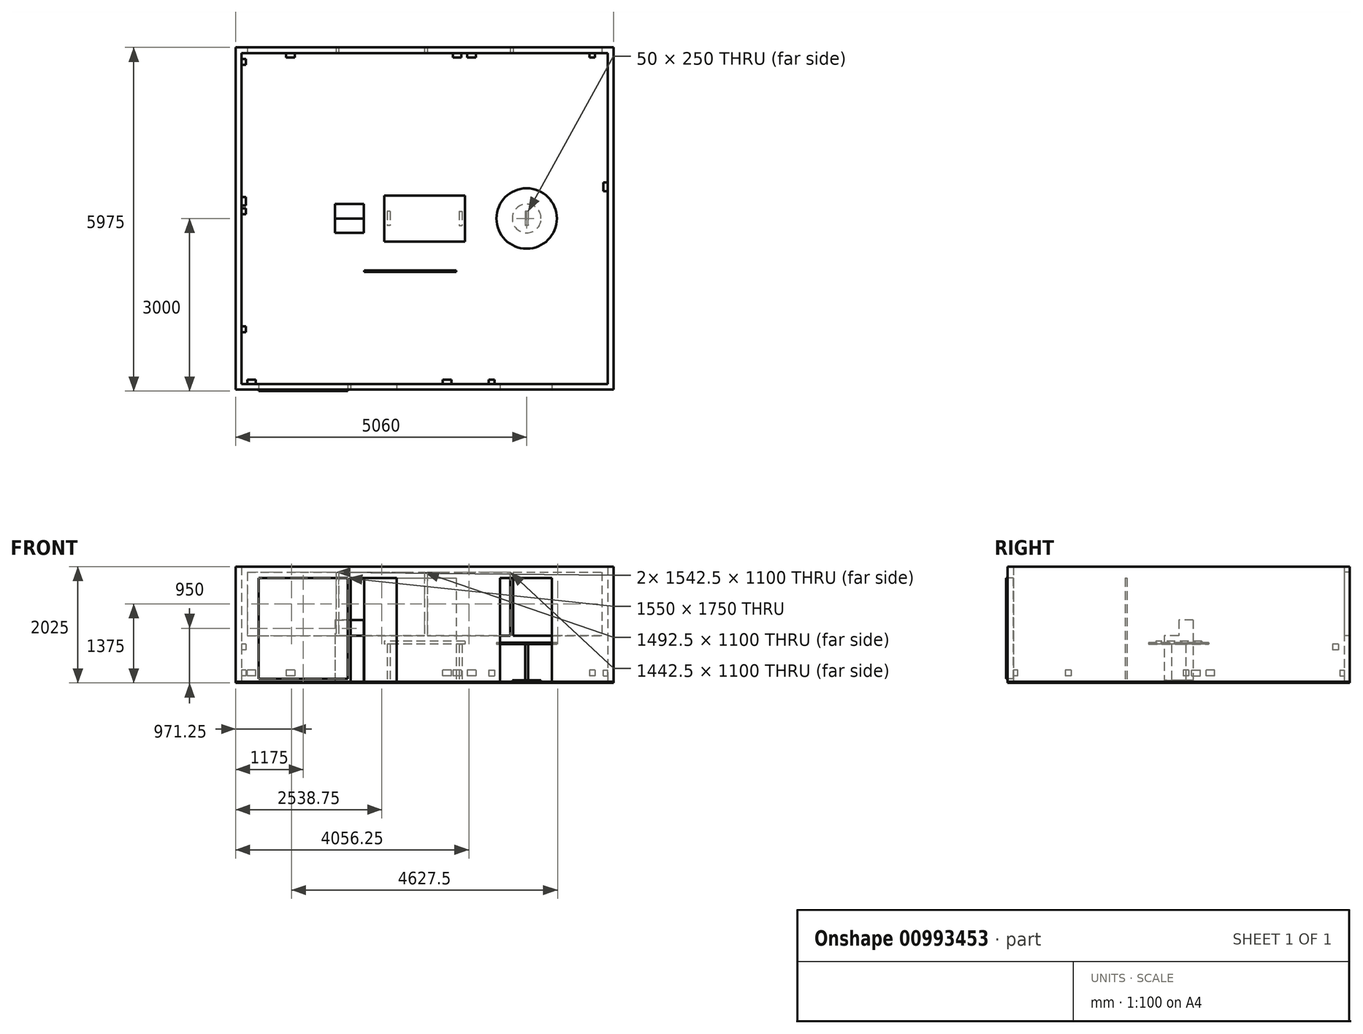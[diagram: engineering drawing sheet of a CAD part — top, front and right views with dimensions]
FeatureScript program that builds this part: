
annotation { "Feature Type Name" : "Feature", "Feature Type Description" : "" }
export const myFeature = defineFeature(function(context is Context, id is Id, definition is map)
    precondition{}
    {
        {
            var Q0;
            Q0=qCreatedBy(makeId("Top.planeOp"),FACE);
            var sketch = newSketch(context, id + "F0", { "sketchPlane" : qUnion([Q0])});
            skLineSegment(sketch, "E0.bottom", {"start": v(3185, 2875) * mm, "end": v(-3185, 2875) * mm});
            skLineSegment(sketch, "E0.top", {"start": v(3185, -2875) * mm, "end": v(-3185, -2875) * mm});
            skLineSegment(sketch, "E0.left", {"start": v(3185, 2875) * mm, "end": v(3185, -2875) * mm});
            skLineSegment(sketch, "E0.right", {"start": v(-3185, 2875) * mm, "end": v(-3185, -2875) * mm});
            skPoint(sketch, "E0.middle", {"position": v(0, 0) * mm});
            skLineSegment(sketch, "E1.0", {"start": v(3285, 2975) * mm, "end": v(-3285, 2975) * mm});
            skLineSegment(sketch, "E1.1", {"start": v(3285, 2975) * mm, "end": v(3285, -2975) * mm});
            skLineSegment(sketch, "E1.2", {"start": v(3285, -2975) * mm, "end": v(-3285, -2975) * mm});
            skLineSegment(sketch, "E1.3", {"start": v(-3285, 2975) * mm, "end": v(-3285, -2975) * mm});
            skSolve(sketch);
        }
        {
            var Q0;
            Q0=makeQuery(id+"F0.imprint","IMPRINT",FACE,{"disambiguationData":[TD([[makeQuery(id+"F0.imprint","IMPRINT",EDGE,{"derivedFrom":sQuery(id+"F0.wireOp",EDGE,"E0.bottom")}),-1.0]])]});
            extrude(context, id + "F1", {"entities" : qUnion([Q0]), "depth" : 2000 * mm, "offsetDistance" : 25 * mm});
        }
        {
            var Q0;
            Q0=makeQuery(id+"F0.imprint","IMPRINT",FACE,{"disambiguationData":[TD([[makeQuery(id+"F0.imprint","IMPRINT",EDGE,{"derivedFrom":sQuery(id+"F0.wireOp",EDGE,"E0.bottom")}),-1.0]])]});
            var Q1;
            Q1=makeQuery(id+"F0.imprint","IMPRINT",FACE,{"disambiguationData":[TD([[makeQuery(id+"F0.imprint","IMPRINT",EDGE,{"derivedFrom":sQuery(id+"F0.wireOp",EDGE,"E0.bottom")}),1.0]])]});
            extrude(context, id + "F2", {"entities" : qUnion([Q0, Q1]), "oppositeDirection" : true, "depth" : 25 * mm, "offsetDistance" : 25 * mm});
        }
        {
            var Q0;
            Q0=makeQuery(id+"F1.opExtrude","SWEPT_FACE",FACE,{"disambiguationData":[OSD([sQuery(id+"F0.wireOp",EDGE,"E1.2")])]});
            var sketch = newSketch(context, id + "F3", { "sketchPlane" : qUnion([Q0])});
            skLineSegment(sketch, "E2.bottom", {"start": v(-1285, 0) * mm, "end": v(-485, 0) * mm});
            skLineSegment(sketch, "E2.top", {"start": v(-1285, 1800) * mm, "end": v(-485, 1800) * mm});
            skLineSegment(sketch, "E2.left", {"start": v(-1285, 0) * mm, "end": v(-1285, 1800) * mm});
            skLineSegment(sketch, "E2.right", {"start": v(-485, 0) * mm, "end": v(-485, 1800) * mm});
            skLineSegment(sketch, "E3.bottom", {"start": v(1315, 0) * mm, "end": v(2215, 0) * mm});
            skLineSegment(sketch, "E3.top", {"start": v(1315, 1800) * mm, "end": v(2215, 1800) * mm});
            skLineSegment(sketch, "E3.left", {"start": v(1315, 0) * mm, "end": v(1315, 1800) * mm});
            skLineSegment(sketch, "E3.right", {"start": v(2215, 0) * mm, "end": v(2215, 1800) * mm});
            skLineSegment(sketch, "E4.bottom", {"start": v(-2885, 1800) * mm, "end": v(-1335, 1800) * mm});
            skLineSegment(sketch, "E4.top", {"start": v(-2885, 50) * mm, "end": v(-1335, 50) * mm});
            skLineSegment(sketch, "E4.left", {"start": v(-2885, 1800) * mm, "end": v(-2885, 50) * mm});
            skLineSegment(sketch, "E4.right", {"start": v(-1335, 1800) * mm, "end": v(-1335, 50) * mm});
            skSolve(sketch);
        }
        {
            var Q0;
            Q0=makeQuery(id+"F3.imprint","IMPRINT",FACE,{"disambiguationData":[TD([[makeQuery(id+"F3.imprint","IMPRINT",EDGE,{"derivedFrom":sQuery(id+"F3.wireOp",EDGE,"E2.bottom")}),-1.0]])]});
            var Q1;
            Q1=makeQuery(id+"F3.imprint","IMPRINT",FACE,{"disambiguationData":[TD([[makeQuery(id+"F3.imprint","IMPRINT",EDGE,{"derivedFrom":sQuery(id+"F3.wireOp",EDGE,"E3.bottom")}),-1.0]])]});
            var Q2;
            Q2=makeQuery(id+"F3.imprint","IMPRINT",FACE,{"disambiguationData":[TD([[makeQuery(id+"F3.imprint","IMPRINT",EDGE,{"derivedFrom":sQuery(id+"F3.wireOp",EDGE,"E4.bottom")}),-1.0]])]});
            var Q3;
            Q3=makeQuery(id+"F1.opExtrude","SWEPT_FACE",FACE,{"disambiguationData":[OSD([sQuery(id+"F0.wireOp",EDGE,"E0.top")])]});
            extrude(context, id + "F4", {"entities" : qUnion([Q0, Q1, Q2]), "operationType" : NewBodyOperationType.REMOVE, "endBound" : BoundingType.UP_TO_SURFACE, "oppositeDirection" : true, "depth" : 220 * mm, "endBoundEntityFace" : qUnion([Q3]), "offsetDistance" : 25 * mm});
        }
        {
            var Q0;
            Q0=makeQuery(id+"F3.imprint","IMPRINT",FACE,{"disambiguationData":[TD([[makeQuery(id+"F3.imprint","IMPRINT",EDGE,{"derivedFrom":sQuery(id+"F3.wireOp",EDGE,"E4.bottom")}),-1.0]])]});
            extrude(context, id + "F5", {"entities" : qUnion([Q0]), "depth" : 25 * mm, "offsetDistance" : 25 * mm});
        }
        {
            var Q0;
            Q0=makeQuery(id+"F1.opExtrude","SWEPT_FACE",FACE,{"disambiguationData":[OSD([sQuery(id+"F0.wireOp",EDGE,"E0.bottom")])]});
            var sketch = newSketch(context, id + "F6", { "sketchPlane" : qUnion([Q0])});
            skLineSegment(sketch, "E5.bottom", {"start": v(-3085, 1900) * mm, "end": v(3085, 1900) * mm});
            skLineSegment(sketch, "E5.top", {"start": v(-3085, 800) * mm, "end": v(3085, 800) * mm});
            skLineSegment(sketch, "E5.left", {"start": v(-3085, 1900) * mm, "end": v(-3085, 800) * mm});
            skLineSegment(sketch, "E5.right", {"start": v(3085, 1900) * mm, "end": v(3085, 800) * mm});
            skLineSegment(sketch, "E6", {"start": v(0, 1900) * mm, "end": v(0, 800) * mm});
            skLineSegment(sketch, "E7", {"start": v(-1542.5, 1900) * mm, "end": v(-1542.5, 800) * mm});
            skLineSegment(sketch, "E8", {"start": v(-1492.5, 1900) * mm, "end": v(-1492.5, 800) * mm});
            skLineSegment(sketch, "E9.MirrorCS", {"start": v(1492.5, 1900) * mm, "end": v(1492.5, 800) * mm});
            skLineSegment(sketch, "E10.MirrorCS", {"start": v(1542.5, 1900) * mm, "end": v(1542.5, 800) * mm});
            skLineSegment(sketch, "E11", {"start": v(50, 1900) * mm, "end": v(50, 800) * mm});
            skSolve(sketch);
        }
        {
            var Q0;
            {var subQ0=sQuery(id+"F6.wireOp",EDGE,"E5.left");Q0=makeQuery(id+"F6.imprint","IMPRINT",FACE,{"disambiguationData":[TD([[makeQuery(id+"F6.imprint","IMPRINT",EDGE,{"derivedFrom":subQ0}),1.0]])]});}
            var Q1;
            {var subQ0=sQuery(id+"F6.wireOp",EDGE,"E6");Q1=makeQuery(id+"F6.imprint","IMPRINT",FACE,{"disambiguationData":[TD([[makeQuery(id+"F6.imprint","IMPRINT",EDGE,{"derivedFrom":subQ0}),-1.0]])]});}
            var Q2;
            {var subQ0=sQuery(id+"F6.wireOp",EDGE,"E9.MirrorCS");Q2=makeQuery(id+"F6.imprint","IMPRINT",FACE,{"disambiguationData":[TD([[makeQuery(id+"F6.imprint","IMPRINT",EDGE,{"derivedFrom":subQ0}),-1.0]])]});}
            var Q3;
            {var subQ0=sQuery(id+"F6.wireOp",EDGE,"E5.right");Q3=makeQuery(id+"F6.imprint","IMPRINT",FACE,{"disambiguationData":[TD([[makeQuery(id+"F6.imprint","IMPRINT",EDGE,{"derivedFrom":subQ0}),-1.0]])]});}
            var Q4;
            Q4=makeQuery(id+"F1.opExtrude","SWEPT_FACE",FACE,{"disambiguationData":[OSD([sQuery(id+"F0.wireOp",EDGE,"E1.0")])]});
            extrude(context, id + "F7", {"entities" : qUnion([Q0, Q1, Q2, Q3]), "operationType" : NewBodyOperationType.REMOVE, "endBound" : BoundingType.UP_TO_SURFACE, "oppositeDirection" : true, "depth" : 25 * mm, "endBoundEntityFace" : qUnion([Q4]), "offsetDistance" : 25 * mm});
        }
        {
            var Q0;
            Q0=qCreatedBy(makeId("Top.planeOp"),FACE);
            var sketch = newSketch(context, id + "F8", { "sketchPlane" : qUnion([Q0])});
            skLineSegment(sketch, "E12.bottom", {"start": v(700, 400) * mm, "end": v(-700, 400) * mm, "construction": true});
            skLineSegment(sketch, "E12.top", {"start": v(700, -400) * mm, "end": v(-700, -400) * mm, "construction": true});
            skLineSegment(sketch, "E12.left", {"start": v(700, 400) * mm, "end": v(700, -400) * mm, "construction": true});
            skLineSegment(sketch, "E12.right", {"start": v(-700, 400) * mm, "end": v(-700, -400) * mm, "construction": true});
            skPoint(sketch, "E12.middle", {"position": v(0, 0) * mm});
            skLineSegment(sketch, "E13.bottom", {"start": v(-600, 125) * mm, "end": v(-650, 125) * mm});
            skLineSegment(sketch, "E13.top", {"start": v(-600, -125) * mm, "end": v(-650, -125) * mm});
            skLineSegment(sketch, "E13.left", {"start": v(-600, 125) * mm, "end": v(-600, -125) * mm});
            skLineSegment(sketch, "E13.right", {"start": v(-650, 125) * mm, "end": v(-650, -125) * mm});
            skPoint(sketch, "E13.middle", {"position": v(-625, 0) * mm});
            skPoint(sketch, "E13.middle.positionSnap0", {"position": v(-700, 0) * mm});
            skPoint(sketch, "E13.centerSnap0", {"position": v(-700, 0) * mm});
            skLineSegment(sketch, "E14.MirrorCS", {"start": v(600, 125) * mm, "end": v(600, -125) * mm});
            skLineSegment(sketch, "E15.MirrorCS", {"start": v(600, 125) * mm, "end": v(650, 125) * mm});
            skLineSegment(sketch, "E16.MirrorCS", {"start": v(650, 125) * mm, "end": v(650, -125) * mm});
            skLineSegment(sketch, "E17.MirrorCS", {"start": v(600, -125) * mm, "end": v(650, -125) * mm});
            skLineSegment(sketch, "E18.bottom", {"start": v(600, 2.5) * mm, "end": v(-600, 2.5) * mm});
            skLineSegment(sketch, "E18.top", {"start": v(600, -2.5) * mm, "end": v(-600, -2.5) * mm});
            skLineSegment(sketch, "E18.left", {"start": v(600, 2.5) * mm, "end": v(600, -2.5) * mm});
            skLineSegment(sketch, "E18.right", {"start": v(-600, 2.5) * mm, "end": v(-600, -2.5) * mm});
            skLineSegment(sketch, "E19", {"start": v(1200, 400) * mm, "end": v(1200, -400) * mm, "construction": true});
            skLineSegment(sketch, "E20.MirrorCS", {"start": v(1750, 125) * mm, "end": v(1750, -125) * mm});
            skLineSegment(sketch, "E21.MirrorCS", {"start": v(1800, 125) * mm, "end": v(1750, 125) * mm});
            skLineSegment(sketch, "E22.MirrorCS", {"start": v(1800, 125) * mm, "end": v(1800, -125) * mm});
            skLineSegment(sketch, "E23.MirrorCS", {"start": v(1800, -125) * mm, "end": v(1750, -125) * mm});
            skCircle(sketch, "E24", {"center": v(1775, 0) * mm, "radius": 250 * mm});
            skPoint(sketch, "E24.centerSnap0", {"position": v(1775, 125) * mm});
            skPoint(sketch, "E24.centerSnap1", {"position": v(1800, 0) * mm});
            skSolve(sketch);
        }
        {
            var Q0;
            {var subQ3=sQuery(id+"F8.wireOp",EDGE,"E13.bottom");Q0=makeQuery(id+"F8.imprint","IMPRINT",FACE,{"disambiguationData":[TD([[makeQuery(id+"F8.imprint","IMPRINT",EDGE,{"derivedFrom":subQ3}),1.0]])]});}
            var Q1;
            {var subQ0=sQuery(id+"F8.wireOp",EDGE,"E15.MirrorCS");Q1=makeQuery(id+"F8.imprint","IMPRINT",FACE,{"disambiguationData":[TD([[makeQuery(id+"F8.imprint","IMPRINT",EDGE,{"derivedFrom":subQ0}),-1.0]])]});}
            extrude(context, id + "F9", {"entities" : qUnion([Q0, Q1]), "depth" : 650 * mm, "offsetDistance" : 25 * mm});
        }
        {
            var Q0;
            Q0=makeQuery(id+"F9.opExtrude","CAP_FACE",FACE,{"disambiguationData":[OSD([sQuery(id+"F8.wireOp",EDGE,"E13.bottom"),sQuery(id+"F8.wireOp",EDGE,"E13.top"),sQuery(id+"F8.wireOp",EDGE,"E13.left"),sQuery(id+"F8.wireOp",EDGE,"E13.right"),sQuery(id+"F8.wireOp",EDGE,"E14.MirrorCS"),sQuery(id+"F8.wireOp",EDGE,"E15.MirrorCS"),sQuery(id+"F8.wireOp",EDGE,"E16.MirrorCS"),sQuery(id+"F8.wireOp",EDGE,"E17.MirrorCS"),sQuery(id+"F8.wireOp",EDGE,"E18.bottom"),sQuery(id+"F8.wireOp",EDGE,"E18.top")])],"isStart":false});
            var sketch = newSketch(context, id + "F10", { "sketchPlane" : qUnion([Q0])});
            skLineSegment(sketch, "E25.0", {"start": v(700, -400) * mm, "end": v(-700, -400) * mm});
            skLineSegment(sketch, "E26.0", {"start": v(-700, 400) * mm, "end": v(-700, -400) * mm});
            skLineSegment(sketch, "E27.0", {"start": v(700, 400) * mm, "end": v(-700, 400) * mm});
            skLineSegment(sketch, "E28.0", {"start": v(700, 400) * mm, "end": v(700, -400) * mm});
            skSolve(sketch);
        }
        {
            var Q0;
            Q0=makeQuery(id+"F10.imprint","IMPRINT",FACE,{"disambiguationData":[TD([[makeQuery(id+"F10.imprint","IMPRINT",EDGE,{"derivedFrom":sQuery(id+"F10.wireOp",EDGE,"E25.0")}),-1.0]])]});
            var Q1;
            {var subQ6=sQuery(id+"F8.wireOp",EDGE,"E13.bottom");Q1=makeQuery(id+"F10.imprint","IMPRINT",FACE,{"disambiguationData":[TD([[makeQuery(id+"F10.imprint","IMPRINT",EDGE,{"derivedFrom":makeQuery(id+"F9.opExtrude","CAP_EDGE",EDGE,{"disambiguationData":[OSD([subQ6])],"isStart":false})}),1.0]])]});}
            var Q2;
            Q2=makeQuery(id+"F10.imprint","IMPRINT",FACE,{"disambiguationData":[TD([[makeQuery(id+"F10.imprint","IMPRINT",EDGE,{"derivedFrom":makeQuery(id+"F9.opExtrude","CAP_EDGE",EDGE,{"disambiguationData":[OSD([sQuery(id+"F8.wireOp",EDGE,"E15.MirrorCS")])],"isStart":false})}),-1.0]])]});
            extrude(context, id + "F11", {"entities" : qUnion([Q0, Q1, Q2]), "operationType" : NewBodyOperationType.ADD, "depth" : 50 * mm, "offsetDistance" : 25 * mm});
        }
        {
            var Q0;
            Q0=makeQuery(id+"F8.imprint","IMPRINT",FACE,{"disambiguationData":[TD([[makeQuery(id+"F8.imprint","IMPRINT",EDGE,{"derivedFrom":sQuery(id+"F8.wireOp",EDGE,"E20.MirrorCS")}),1.0]])]});
            extrude(context, id + "F12", {"entities" : qUnion([Q0]), "depth" : 650 * mm, "offsetDistance" : 25 * mm});
        }
        {
            var Q0;
            Q0=makeQuery(id+"F8.imprint","IMPRINT",FACE,{"disambiguationData":[TD([[makeQuery(id+"F8.imprint","IMPRINT",EDGE,{"derivedFrom":sQuery(id+"F8.wireOp",EDGE,"E20.MirrorCS")}),-1.0]])]});
            extrude(context, id + "F13", {"entities" : qUnion([Q0]), "operationType" : NewBodyOperationType.ADD, "depth" : 25 * mm, "offsetDistance" : 25 * mm});
        }
        {
            var Q0;
            Q0=makeQuery(id+"F12.opExtrude","CAP_FACE",FACE,{"disambiguationData":[OSD([sQuery(id+"F8.wireOp",EDGE,"E20.MirrorCS"),sQuery(id+"F8.wireOp",EDGE,"E21.MirrorCS"),sQuery(id+"F8.wireOp",EDGE,"E22.MirrorCS"),sQuery(id+"F8.wireOp",EDGE,"E23.MirrorCS")])],"isStart":false});
            var sketch = newSketch(context, id + "F14", { "sketchPlane" : qUnion([Q0])});
            skCircle(sketch, "E29", {"center": v(1775, 0) * mm, "radius": 525 * mm});
            skPoint(sketch, "E29.centerSnap0", {"position": v(1775, 125) * mm});
            skPoint(sketch, "E29.centerSnap1", {"position": v(1800, 0) * mm});
            skSolve(sketch);
        }
        {
            var Q0;
            Q0=makeQuery(id+"F14.imprint","IMPRINT",FACE,{"disambiguationData":[TD([[makeQuery(id+"F14.imprint","IMPRINT",EDGE,{"derivedFrom":sQuery(id+"F14.wireOp",EDGE,"E29")}),1.0]])]});
            var Q1;
            Q1=makeQuery(id+"F14.imprint","IMPRINT",FACE,{"disambiguationData":[TD([[makeQuery(id+"F14.imprint","IMPRINT",EDGE,{"derivedFrom":makeQuery(id+"F12.opExtrude","CAP_EDGE",EDGE,{"disambiguationData":[OSD([sQuery(id+"F8.wireOp",EDGE,"E20.MirrorCS")])],"isStart":false})}),1.0]])]});
            extrude(context, id + "F15", {"entities" : qUnion([Q0, Q1]), "operationType" : NewBodyOperationType.ADD, "depth" : 25 * mm, "offsetDistance" : 25 * mm});
        }
        {
            var Q0;
            Q0=makeQuery(id+"F1.opExtrude","SWEPT_FACE",FACE,{"disambiguationData":[OSD([sQuery(id+"F0.wireOp",EDGE,"E0.right")])]});
            var sketch = newSketch(context, id + "F16", { "sketchPlane" : qUnion([Q0])});
            skLineSegment(sketch, "E30.bottom", {"start": v(2775, 650) * mm, "end": v(2675, 650) * mm});
            skLineSegment(sketch, "E30.top", {"start": v(2775, 550) * mm, "end": v(2675, 550) * mm});
            skLineSegment(sketch, "E30.left", {"start": v(2775, 650) * mm, "end": v(2775, 550) * mm});
            skLineSegment(sketch, "E30.right", {"start": v(2675, 650) * mm, "end": v(2675, 550) * mm});
            skPoint(sketch, "E30.middle", {"position": v(2725, 600) * mm});
            skLineSegment(sketch, "E31.bottom", {"start": v(175, 200) * mm, "end": v(75, 200) * mm});
            skLineSegment(sketch, "E31.top", {"start": v(175, 100) * mm, "end": v(75, 100) * mm});
            skLineSegment(sketch, "E31.left", {"start": v(175, 200) * mm, "end": v(175, 100) * mm});
            skLineSegment(sketch, "E31.right", {"start": v(75, 200) * mm, "end": v(75, 100) * mm});
            skLineSegment(sketch, "E32.bottom", {"start": v(225, 100) * mm, "end": v(375, 100) * mm});
            skLineSegment(sketch, "E32.top", {"start": v(225, 200) * mm, "end": v(375, 200) * mm});
            skLineSegment(sketch, "E32.left", {"start": v(225, 100) * mm, "end": v(225, 200) * mm});
            skLineSegment(sketch, "E32.right", {"start": v(375, 100) * mm, "end": v(375, 200) * mm});
            skLineSegment(sketch, "E33.bottom", {"start": v(-1875, 200) * mm, "end": v(-1975, 200) * mm});
            skLineSegment(sketch, "E33.top", {"start": v(-1875, 100) * mm, "end": v(-1975, 100) * mm});
            skLineSegment(sketch, "E33.left", {"start": v(-1875, 200) * mm, "end": v(-1875, 100) * mm});
            skLineSegment(sketch, "E33.right", {"start": v(-1975, 200) * mm, "end": v(-1975, 100) * mm});
            skSolve(sketch);
        }
        {
            var Q0;
            Q0 = qSketchRegion(id + "F16", true);
            extrude(context, id + "F17", {"entities" : qUnion([Q0]), "operationType" : NewBodyOperationType.ADD, "depth" : 75 * mm, "offsetDistance" : 25 * mm});
        }
        {
            var Q0;
            Q0=makeQuery(id+"F1.opExtrude","SWEPT_FACE",FACE,{"disambiguationData":[OSD([sQuery(id+"F0.wireOp",EDGE,"E0.top")])]});
            var sketch = newSketch(context, id + "F18", { "sketchPlane" : qUnion([Q0])});
            skLineSegment(sketch, "E34.bottom", {"start": v(2935, 100) * mm, "end": v(3085, 100) * mm});
            skLineSegment(sketch, "E34.top", {"start": v(2935, 200) * mm, "end": v(3085, 200) * mm});
            skLineSegment(sketch, "E34.left", {"start": v(2935, 100) * mm, "end": v(2935, 200) * mm});
            skLineSegment(sketch, "E34.right", {"start": v(3085, 100) * mm, "end": v(3085, 200) * mm});
            skLineSegment(sketch, "E35.bottom", {"start": v(-465, 100) * mm, "end": v(-315, 100) * mm});
            skLineSegment(sketch, "E35.top", {"start": v(-465, 200) * mm, "end": v(-315, 200) * mm});
            skLineSegment(sketch, "E35.left", {"start": v(-465, 100) * mm, "end": v(-465, 200) * mm});
            skLineSegment(sketch, "E35.right", {"start": v(-315, 100) * mm, "end": v(-315, 200) * mm});
            skLineSegment(sketch, "E36.bottom", {"start": v(-1115, 200) * mm, "end": v(-1215, 200) * mm});
            skLineSegment(sketch, "E36.top", {"start": v(-1115, 100) * mm, "end": v(-1215, 100) * mm});
            skLineSegment(sketch, "E36.left", {"start": v(-1115, 200) * mm, "end": v(-1115, 100) * mm});
            skLineSegment(sketch, "E36.right", {"start": v(-1215, 200) * mm, "end": v(-1215, 100) * mm});
            skPoint(sketch, "E36.middle", {"position": v(-1165, 150) * mm});
            skPoint(sketch, "E36.middle.positionSnap0", {"position": v(-465, 150) * mm});
            skPoint(sketch, "E36.centerSnap0", {"position": v(-465, 150) * mm});
            skSolve(sketch);
        }
        {
            var Q0;
            Q0 = qSketchRegion(id + "F18", true);
            var Q1;
            Q1 = qConstructionFilter(qBodyType(qCreatedBy(id + "F18" ,EDGE), BodyType.WIRE), ConstructionObject.NO);
            extrude(context, id + "F19", {"entities" : qUnion([Q0]), "operationType" : NewBodyOperationType.ADD, "surfaceEntities" : qUnion([Q1]), "depth" : 75 * mm, "offsetDistance" : 25 * mm});
        }
        {
            var Q0;
            Q0=makeQuery(id+"F1.opExtrude","SWEPT_FACE",FACE,{"disambiguationData":[OSD([sQuery(id+"F0.wireOp",EDGE,"E0.left")])]});
            var sketch = newSketch(context, id + "F20", { "sketchPlane" : qUnion([Q0])});
            skLineSegment(sketch, "E37.bottom", {"start": v(-625, 100) * mm, "end": v(-475, 100) * mm});
            skLineSegment(sketch, "E37.top", {"start": v(-625, 200) * mm, "end": v(-475, 200) * mm});
            skLineSegment(sketch, "E37.left", {"start": v(-625, 100) * mm, "end": v(-625, 200) * mm});
            skLineSegment(sketch, "E37.right", {"start": v(-475, 100) * mm, "end": v(-475, 200) * mm});
            skSolve(sketch);
        }
        {
            var Q0;
            Q0 = qSketchRegion(id + "F20", true);
            extrude(context, id + "F21", {"entities" : qUnion([Q0]), "operationType" : NewBodyOperationType.ADD, "depth" : 75 * mm, "offsetDistance" : 25 * mm});
        }
        {
            var Q0;
            Q0=makeQuery(id+"F1.opExtrude","SWEPT_FACE",FACE,{"disambiguationData":[OSD([sQuery(id+"F0.wireOp",EDGE,"E0.bottom")])]});
            var sketch = newSketch(context, id + "F22", { "sketchPlane" : qUnion([Q0])});
            skLineSegment(sketch, "E38.bottom", {"start": v(-2260, 200) * mm, "end": v(-2410, 200) * mm});
            skLineSegment(sketch, "E38.top", {"start": v(-2260, 100) * mm, "end": v(-2410, 100) * mm});
            skLineSegment(sketch, "E38.left", {"start": v(-2260, 200) * mm, "end": v(-2260, 100) * mm});
            skLineSegment(sketch, "E38.right", {"start": v(-2410, 200) * mm, "end": v(-2410, 100) * mm});
            skPoint(sketch, "E38.middle", {"position": v(-2335, 150) * mm});
            skLineSegment(sketch, "E39.bottom", {"start": v(640, 200) * mm, "end": v(490, 200) * mm});
            skLineSegment(sketch, "E39.top", {"start": v(640, 100) * mm, "end": v(490, 100) * mm});
            skLineSegment(sketch, "E39.left", {"start": v(640, 200) * mm, "end": v(640, 100) * mm});
            skLineSegment(sketch, "E39.right", {"start": v(490, 200) * mm, "end": v(490, 100) * mm});
            skPoint(sketch, "E39.middle", {"position": v(565, 150) * mm});
            skPoint(sketch, "E39.middle.positionSnap0", {"position": v(-2260, 150) * mm});
            skPoint(sketch, "E39.centerSnap0", {"position": v(-2260, 150) * mm});
            skLineSegment(sketch, "E40.bottom", {"start": v(890, 200) * mm, "end": v(740, 200) * mm});
            skLineSegment(sketch, "E40.top", {"start": v(890, 100) * mm, "end": v(740, 100) * mm});
            skLineSegment(sketch, "E40.left", {"start": v(890, 200) * mm, "end": v(890, 100) * mm});
            skLineSegment(sketch, "E40.right", {"start": v(740, 200) * mm, "end": v(740, 100) * mm});
            skPoint(sketch, "E40.middle", {"position": v(815, 150) * mm});
            skPoint(sketch, "E40.middle.positionSnap0", {"position": v(640, 150) * mm});
            skPoint(sketch, "E40.centerSnap0", {"position": v(640, 150) * mm});
            skLineSegment(sketch, "E41.bottom", {"start": v(2965, 200) * mm, "end": v(2865, 200) * mm});
            skLineSegment(sketch, "E41.top", {"start": v(2965, 100) * mm, "end": v(2865, 100) * mm});
            skLineSegment(sketch, "E41.left", {"start": v(2965, 200) * mm, "end": v(2965, 100) * mm});
            skLineSegment(sketch, "E41.right", {"start": v(2865, 200) * mm, "end": v(2865, 100) * mm});
            skPoint(sketch, "E41.middle", {"position": v(2915, 150) * mm});
            skPoint(sketch, "E41.middle.positionSnap0", {"position": v(890, 150) * mm});
            skPoint(sketch, "E41.centerSnap0", {"position": v(890, 150) * mm});
            skSolve(sketch);
        }
        {
            var Q0;
            Q0 = qSketchRegion(id + "F22", true);
            extrude(context, id + "F23", {"entities" : qUnion([Q0]), "operationType" : NewBodyOperationType.ADD, "depth" : 75 * mm, "offsetDistance" : 25 * mm});
        }
        {
            var Q0;
            Q0=makeQuery(id+"F0.imprint","IMPRINT",FACE,{"disambiguationData":[TD([[makeQuery(id+"F0.imprint","IMPRINT",EDGE,{"derivedFrom":sQuery(id+"F0.wireOp",EDGE,"E0.bottom")}),1.0]])]});
            var sketch = newSketch(context, id + "F24", { "sketchPlane" : qUnion([Q0])});
            skLineSegment(sketch, "E42.bottom", {"start": v(-1059.25, 250) * mm, "end": v(-1559.25, 250) * mm});
            skLineSegment(sketch, "E42.top", {"start": v(-1059.25, -250) * mm, "end": v(-1559.25, -250) * mm});
            skLineSegment(sketch, "E42.left", {"start": v(-1059.25, 250) * mm, "end": v(-1059.25, -250) * mm});
            skLineSegment(sketch, "E42.right", {"start": v(-1559.25, 250) * mm, "end": v(-1559.25, -250) * mm});
            skPoint(sketch, "E42.middle", {"position": v(-1309.25, 0) * mm});
            skSolve(sketch);
        }
        {
            var Q0;
            Q0 = qSketchRegion(id + "F24", true);
            extrude(context, id + "F25", {"entities" : qUnion([Q0]), "depth" : 800 * mm, "offsetDistance" : 25 * mm});
        }
        {
            var Q0;
            Q0=makeQuery(id+"F25.opExtrude","CAP_FACE",FACE,{"disambiguationData":[OSD([sQuery(id+"F24.wireOp",EDGE,"E42.bottom"),sQuery(id+"F24.wireOp",EDGE,"E42.top"),sQuery(id+"F24.wireOp",EDGE,"E42.left"),sQuery(id+"F24.wireOp",EDGE,"E42.right")])],"isStart":false});
            var sketch = newSketch(context, id + "F26", { "sketchPlane" : qUnion([Q0])});
            skLineSegment(sketch, "E43.bottom", {"start": v(-1559.25, 250) * mm, "end": v(-1059.25, 250) * mm});
            skLineSegment(sketch, "E43.top", {"start": v(-1559.25, 0) * mm, "end": v(-1059.25, 0) * mm});
            skLineSegment(sketch, "E43.left", {"start": v(-1559.25, 250) * mm, "end": v(-1559.25, 0) * mm});
            skLineSegment(sketch, "E43.right", {"start": v(-1059.25, 250) * mm, "end": v(-1059.25, 0) * mm});
            skSolve(sketch);
        }
        {
            var Q0;
            Q0=makeQuery(id+"F26.imprint","IMPRINT",FACE,{"disambiguationData":[TD([[makeQuery(id+"F26.imprint","IMPRINT",EDGE,{"derivedFrom":sQuery(id+"F26.wireOp",EDGE,"E43.bottom")}),1.0]])]});
            extrude(context, id + "F27", {"entities" : qUnion([Q0]), "operationType" : NewBodyOperationType.ADD, "depth" : 270 * mm, "offsetDistance" : 25 * mm});
        }
        {
            var Q0;
            Q0=makeQuery(id+"F0.imprint","IMPRINT",FACE,{"disambiguationData":[TD([[makeQuery(id+"F0.imprint","IMPRINT",EDGE,{"derivedFrom":sQuery(id+"F0.wireOp",EDGE,"E0.bottom")}),1.0]])]});
            var sketch = newSketch(context, id + "F28", { "sketchPlane" : qUnion([Q0])});
            skLineSegment(sketch, "E44.bottom", {"start": v(-1048.18, -930.46) * mm, "end": v(551.82, -930.46) * mm});
            skLineSegment(sketch, "E44.top", {"start": v(-1048.18, -900.46) * mm, "end": v(551.82, -900.46) * mm});
            skLineSegment(sketch, "E44.left", {"start": v(-1048.18, -930.46) * mm, "end": v(-1048.18, -900.46) * mm});
            skLineSegment(sketch, "E44.right", {"start": v(551.82, -930.46) * mm, "end": v(551.82, -900.46) * mm});
            skPoint(sketch, "E44.middle", {"position": v(-248.18, -915.46) * mm});
            skSolve(sketch);
        }
        {
            var Q0;
            Q0 = qSketchRegion(id + "F28", true);
            extrude(context, id + "F29", {"entities" : qUnion([Q0]), "depth" : 1800 * mm, "offsetDistance" : 25 * mm});
        }
    });
